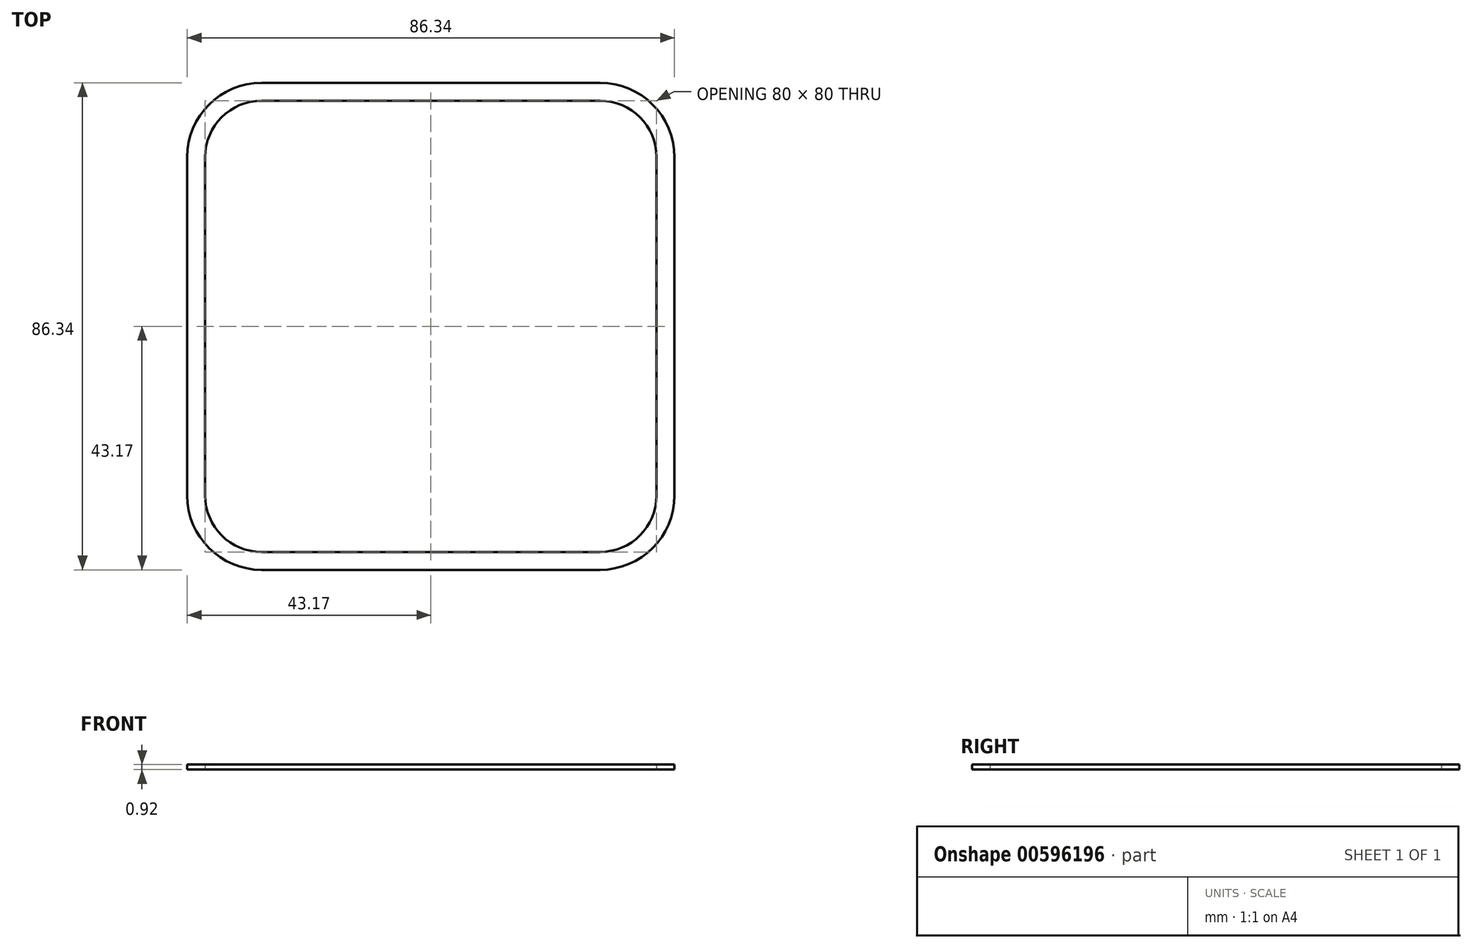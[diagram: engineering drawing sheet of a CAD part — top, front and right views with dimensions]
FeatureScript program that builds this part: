
annotation { "Feature Type Name" : "Feature", "Feature Type Description" : "" }
export const myFeature = defineFeature(function(context is Context, id is Id, definition is map)
    precondition{}
    {
        {
            assignVariable(context, id + "F0", {"name" : "t", "anyValue" : 0.92});
        }
        {
            assignVariable(context, id + "F1", {"name" : "profundidad", "anyValue" : 0.5});
        }
        {
            var Q0;
            Q0=qCreatedBy(makeId("Top.planeOp"),FACE);
            var sketch = newSketch(context, id + "F2", { "sketchPlane" : qUnion([Q0])});
            skLineSegment(sketch, "E0.bottom", {"start": v(30, 40) * mm, "end": v(-30, 40) * mm});
            skLineSegment(sketch, "E0.top", {"start": v(30, -40) * mm, "end": v(-30, -40) * mm});
            skLineSegment(sketch, "E0.left", {"start": v(40, 30) * mm, "end": v(40, -30) * mm});
            skLineSegment(sketch, "E0.right", {"start": v(-40, 30) * mm, "end": v(-40, -30) * mm});
            skPoint(sketch, "E0.middle", {"position": v(0, 0) * mm});
            skPoint(sketch, "E1.visualSharp", {"position": v(-40, 40) * mm});
            skArc(sketch, "E1.filletArc", {"start": v(-30, 40) * mm, "mid": v(-37.07, 37.07) * mm, "end": v(-40, 30) * mm});
            skPoint(sketch, "E2.visualSharp", {"position": v(40, 40) * mm});
            skArc(sketch, "E2.filletArc", {"start": v(40, 30) * mm, "mid": v(37.07, 37.07) * mm, "end": v(30, 40) * mm});
            skPoint(sketch, "E3.visualSharp", {"position": v(40, -40) * mm});
            skArc(sketch, "E3.filletArc", {"start": v(30, -40) * mm, "mid": v(37.07, -37.07) * mm, "end": v(40, -30) * mm});
            skPoint(sketch, "E4.visualSharp", {"position": v(-40, -40) * mm});
            skArc(sketch, "E4.filletArc", {"start": v(-40, -30) * mm, "mid": v(-37.07, -37.07) * mm, "end": v(-30, -40) * mm});
            skArc(sketch, "E5.0", {"start": v(43.17, 30) * mm, "mid": v(39.32, 39.32) * mm, "end": v(30, 43.17) * mm});
            skLineSegment(sketch, "E5.1", {"start": v(43.17, 30) * mm, "end": v(43.18, -30) * mm});
            skLineSegment(sketch, "E5.2", {"start": v(30, 43.17) * mm, "end": v(-30, 43.17) * mm});
            skArc(sketch, "E5.3", {"start": v(30, -43.18) * mm, "mid": v(39.32, -39.32) * mm, "end": v(43.17, -30) * mm});
            skArc(sketch, "E5.4", {"start": v(-30, 43.17) * mm, "mid": v(-39.32, 39.32) * mm, "end": v(-43.18, 30) * mm});
            skLineSegment(sketch, "E5.5", {"start": v(-43.18, 30) * mm, "end": v(-43.17, -30) * mm});
            skArc(sketch, "E5.6", {"start": v(-43.17, -30) * mm, "mid": v(-39.32, -39.32) * mm, "end": v(-30, -43.18) * mm});
            skLineSegment(sketch, "E5.7", {"start": v(30, -43.18) * mm, "end": v(-30, -43.18) * mm});
            skSolve(sketch);
        }
        {
            var Q0;
            Q0 = qSketchRegion(id + "F2", true);
            extrude(context, id + "F3", {"entities" : qUnion([Q0]), "depth" : (getVariable(context, 't')) * mm, "offsetDistance" : 25 * mm});
        }
        {
            var Q0;
            Q0=makeQuery(id+"F3.opExtrude","CAP_FACE",FACE,{"disambiguationData":[OSD([sQuery(id+"F2.wireOp",EDGE,"E0.bottom"),sQuery(id+"F2.wireOp",EDGE,"E0.top"),sQuery(id+"F2.wireOp",EDGE,"E0.left"),sQuery(id+"F2.wireOp",EDGE,"E0.right")])],"isStart":false});
            var sketch = newSketch(context, id + "F4", { "sketchPlane" : qUnion([Q0])});
            skLineSegment(sketch, "E6", {"start": v(-21.35, -30) * mm, "end": v(-21.35, 30) * mm});
            skLineSegment(sketch, "E7", {"start": v(-15, 30) * mm, "end": v(-15, 3.17) * mm});
            skLineSegment(sketch, "E8", {"start": v(-15, 3.17) * mm, "end": v(15, 3.18) * mm});
            skLineSegment(sketch, "E9", {"start": v(15, 3.18) * mm, "end": v(15, 30) * mm});
            skLineSegment(sketch, "E10", {"start": v(21.35, 30) * mm, "end": v(21.35, -30) * mm});
            skLineSegment(sketch, "E11", {"start": v(15, -30) * mm, "end": v(15, -3.17) * mm});
            skLineSegment(sketch, "E12", {"start": v(15, -3.17) * mm, "end": v(-15, -3.18) * mm});
            skLineSegment(sketch, "E13", {"start": v(-15, -3.18) * mm, "end": v(-15, -30) * mm});
            skArc(sketch, "E14", {"start": v(-15, 30) * mm, "mid": v(-18.17, 33.17) * mm, "end": v(-21.35, 30) * mm});
            skArc(sketch, "E15", {"start": v(-21.35, -30) * mm, "mid": v(-18.18, -33.18) * mm, "end": v(-15, -30) * mm});
            skArc(sketch, "E16", {"start": v(15, -30) * mm, "mid": v(18.18, -33.18) * mm, "end": v(21.35, -30) * mm});
            skArc(sketch, "E17", {"start": v(21.35, 30) * mm, "mid": v(18.17, 33.18) * mm, "end": v(15, 30) * mm});
            skLineSegment(sketch, "E18", {"start": v(-40, 0) * mm, "end": v(40, 0) * mm, "construction": true});
            skLineSegment(sketch, "E19", {"start": v(0, 40) * mm, "end": v(0, -40) * mm, "construction": true});
            skSolve(sketch);
        }
        {
            var Q0;
            Q0 = qSketchRegion(id + "F4", true);
            extrude(context, id + "F5", {"entities" : qUnion([Q0]), "operationType" : NewBodyOperationType.REMOVE, "oppositeDirection" : true, "depth" : (getVariable(context, 'profundidad')) * mm, "offsetDistance" : 25 * mm});
        }
        {
            var Q0;
            Q0=makeQuery(id+"F3.opExtrude","CAP_FACE",FACE,{"disambiguationData":[OSD([sQuery(id+"F2.wireOp",EDGE,"E0.bottom"),sQuery(id+"F2.wireOp",EDGE,"E0.top"),sQuery(id+"F2.wireOp",EDGE,"E0.left"),sQuery(id+"F2.wireOp",EDGE,"E0.right")])],"isStart":false});
            var sketch = newSketch(context, id + "F6", { "sketchPlane" : qUnion([Q0])});
            skCircle(sketch, "E20", {"center": v(-50, 50) * mm, "radius": 3.18 * mm});
            skLineSegment(sketch, "E21", {"start": v(0, 40) * mm, "end": v(0, -40) * mm, "construction": true});
            skLineSegment(sketch, "E22", {"start": v(40, 0) * mm, "end": v(-40, 0) * mm, "construction": true});
            skCircle(sketch, "E23.MirrorC", {"center": v(50, 50) * mm, "radius": 3.18 * mm});
            skCircle(sketch, "E24.MirrorC", {"center": v(50, -50) * mm, "radius": 3.18 * mm});
            skCircle(sketch, "E25.MirrorC", {"center": v(-50, -50) * mm, "radius": 3.18 * mm});
            skSolve(sketch);
        }
        {
            var Q0;
            Q0 = qSketchRegion(id + "F6", true);
            extrude(context, id + "F7", {"entities" : qUnion([Q0]), "operationType" : NewBodyOperationType.REMOVE, "endBound" : BoundingType.THROUGH_ALL, "oppositeDirection" : true, "depth" : 25 * mm, "offsetDistance" : 25 * mm});
        }
    });
